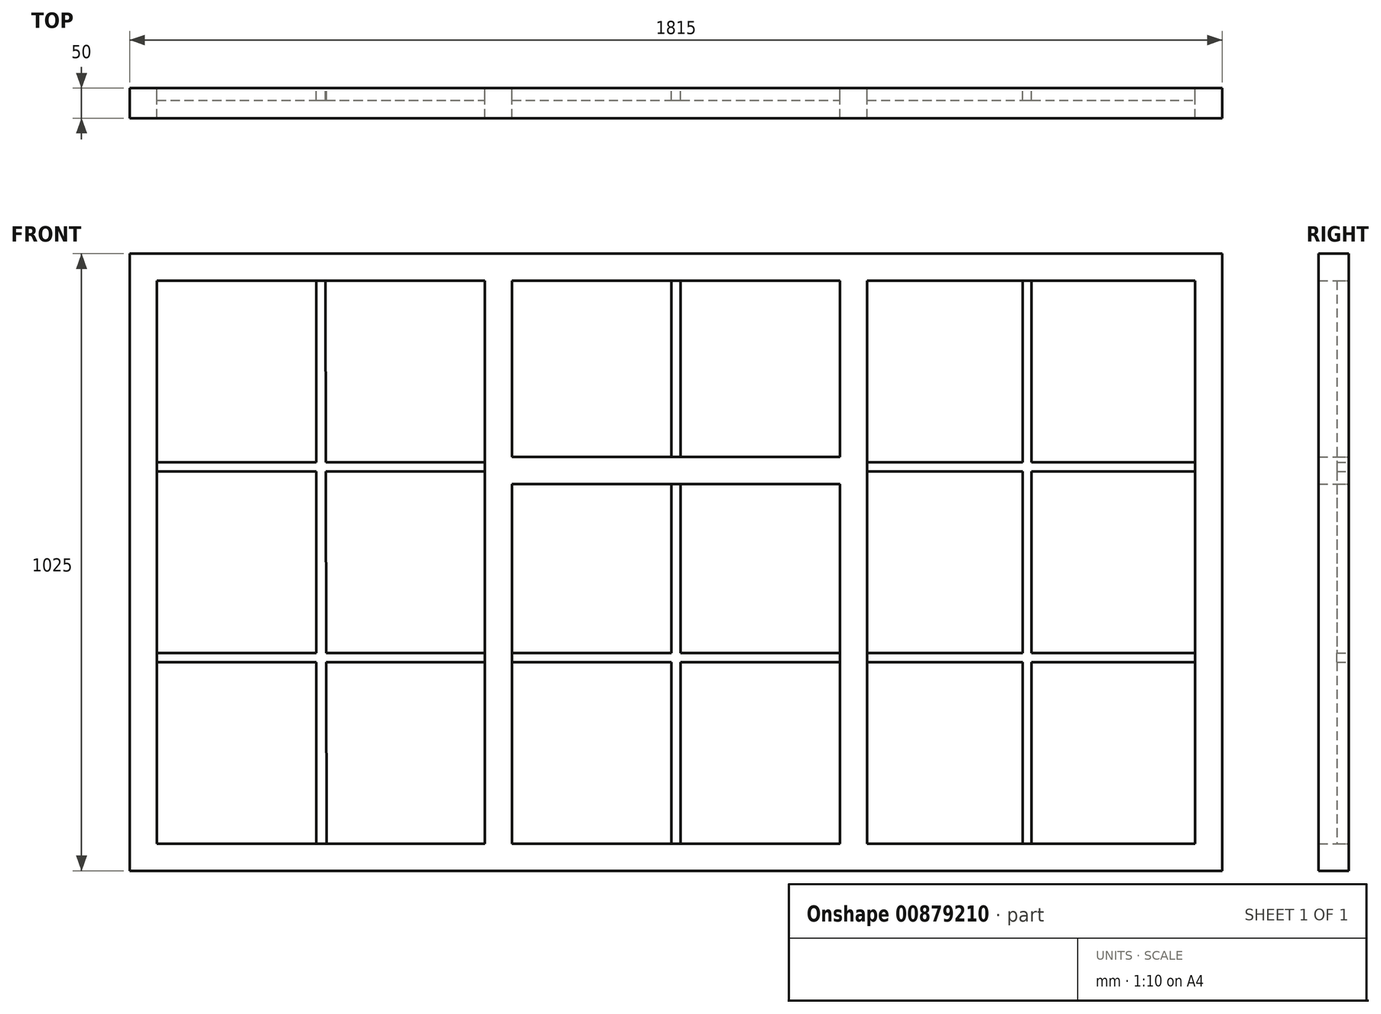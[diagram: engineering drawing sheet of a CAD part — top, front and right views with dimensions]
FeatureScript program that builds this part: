
annotation { "Feature Type Name" : "Feature", "Feature Type Description" : "" }
export const myFeature = defineFeature(function(context is Context, id is Id, definition is map)
    precondition{}
    {
        {
            var Q0;
            Q0=qCreatedBy(makeId("Front.planeOp"),FACE);
            var sketch = newSketch(context, id + "F0", { "sketchPlane" : qUnion([Q0])});
            skLineSegment(sketch, "E0.bottom", {"start": v(0, 0) * mm, "end": v(1815, 0) * mm});
            skLineSegment(sketch, "E0.top", {"start": v(0, 1025) * mm, "end": v(1815, 1025) * mm});
            skLineSegment(sketch, "E0.left", {"start": v(0, 0) * mm, "end": v(0, 1025) * mm});
            skLineSegment(sketch, "E0.right", {"start": v(1815, 0) * mm, "end": v(1815, 1025) * mm});
            skLineSegment(sketch, "E1.bottom", {"start": v(45, 980) * mm, "end": v(590, 980) * mm});
            skLineSegment(sketch, "E1.top", {"start": v(45, 45) * mm, "end": v(590, 45) * mm});
            skLineSegment(sketch, "E1.left", {"start": v(45, 980) * mm, "end": v(45, 45) * mm});
            skLineSegment(sketch, "E1.right", {"start": v(590, 980) * mm, "end": v(590, 45) * mm});
            skLineSegment(sketch, "E2.bottom", {"start": v(635, 980) * mm, "end": v(1180, 980) * mm});
            skLineSegment(sketch, "E2.top", {"start": v(635, 687.5) * mm, "end": v(1180, 687.5) * mm});
            skLineSegment(sketch, "E2.left", {"start": v(635, 980) * mm, "end": v(635, 687.5) * mm});
            skLineSegment(sketch, "E2.right", {"start": v(1180, 980) * mm, "end": v(1180, 687.5) * mm});
            skLineSegment(sketch, "E3.bottom", {"start": v(635, 642.5) * mm, "end": v(1180, 642.5) * mm});
            skLineSegment(sketch, "E3.top", {"start": v(635, 45) * mm, "end": v(1180, 45) * mm});
            skLineSegment(sketch, "E3.left", {"start": v(635, 642.5) * mm, "end": v(635, 45) * mm});
            skLineSegment(sketch, "E3.right", {"start": v(1180, 642.5) * mm, "end": v(1180, 45) * mm});
            skLineSegment(sketch, "E4.bottom", {"start": v(1225, 980) * mm, "end": v(1770, 980) * mm});
            skLineSegment(sketch, "E4.top", {"start": v(1225, 45) * mm, "end": v(1770, 45) * mm});
            skLineSegment(sketch, "E4.left", {"start": v(1225, 980) * mm, "end": v(1225, 45) * mm});
            skLineSegment(sketch, "E4.right", {"start": v(1770, 980) * mm, "end": v(1770, 45) * mm});
            skSolve(sketch);
        }
        {
            var Q0;
            Q0=qSketchRegion(id+"F0",true);
            extrude(context, id + "F1", {"entities" : qUnion([Q0]), "depth" : 50 * mm, "offsetDistance" : 25 * mm});
        }
        {
            var Q0;
            Q0=qCreatedBy(makeId("Front.planeOp"),FACE);
            var sketch = newSketch(context, id + "F2", { "sketchPlane" : qUnion([Q0])});
            skLineSegment(sketch, "E5.bottom", {"start": v(310, 980) * mm, "end": v(325, 980) * mm});
            skLineSegment(sketch, "E5.top", {"start": v(310, 45) * mm, "end": v(327.01, 45) * mm});
            skLineSegment(sketch, "E6.bottom", {"start": v(45, 678.33) * mm, "end": v(310, 678.33) * mm});
            skLineSegment(sketch, "E6.top", {"start": v(45, 663.33) * mm, "end": v(310, 663.33) * mm});
            skLineSegment(sketch, "E6.left", {"start": v(45, 678.33) * mm, "end": v(45, 663.33) * mm});
            skLineSegment(sketch, "E6.right", {"start": v(590, 678.33) * mm, "end": v(590, 663.33) * mm});
            skLineSegment(sketch, "E7.bottom", {"start": v(45, 361.67) * mm, "end": v(310, 361.67) * mm});
            skLineSegment(sketch, "E7.top", {"start": v(45, 346.67) * mm, "end": v(310, 346.67) * mm});
            skLineSegment(sketch, "E7.left", {"start": v(45, 361.67) * mm, "end": v(45, 346.67) * mm});
            skLineSegment(sketch, "E7.right", {"start": v(590, 361.67) * mm, "end": v(590, 346.67) * mm});
            skLineSegment(sketch, "E8.trimOffspring", {"start": v(325, 980) * mm, "end": v(325.65, 678.33) * mm});
            skLineSegment(sketch, "E9.trimOffspring", {"start": v(310, 980) * mm, "end": v(310, 678.33) * mm});
            skLineSegment(sketch, "E10.trimOffspring", {"start": v(325.65, 678.33) * mm, "end": v(590, 678.33) * mm});
            skLineSegment(sketch, "E11.trimOffspring", {"start": v(310, 663.33) * mm, "end": v(310, 361.67) * mm});
            skLineSegment(sketch, "E12.trimOffspring", {"start": v(325.68, 663.33) * mm, "end": v(590, 663.33) * mm});
            skLineSegment(sketch, "E13.trimOffspring", {"start": v(325.68, 663.33) * mm, "end": v(326.33, 361.67) * mm});
            skLineSegment(sketch, "E14.trimOffspring", {"start": v(326.33, 361.67) * mm, "end": v(590, 361.67) * mm});
            skLineSegment(sketch, "E15.trimOffspring", {"start": v(310, 346.67) * mm, "end": v(310, 45) * mm});
            skLineSegment(sketch, "E16.trimOffspring", {"start": v(326.36, 346.67) * mm, "end": v(590, 346.67) * mm});
            skLineSegment(sketch, "E17.trimOffspring", {"start": v(326.36, 346.67) * mm, "end": v(327.01, 45) * mm});
            skLineSegment(sketch, "E18.bottom", {"start": v(1483.1, 980) * mm, "end": v(1498.1, 980) * mm});
            skLineSegment(sketch, "E18.top", {"start": v(1483.1, 45) * mm, "end": v(1498.1, 45) * mm});
            skLineSegment(sketch, "E18.left", {"start": v(1483.1, 980) * mm, "end": v(1483.1, 678.33) * mm});
            skLineSegment(sketch, "E18.right", {"start": v(1498.1, 980) * mm, "end": v(1498.1, 678.33) * mm});
            skLineSegment(sketch, "E19.bottom", {"start": v(1225, 678.33) * mm, "end": v(1483.1, 678.33) * mm});
            skLineSegment(sketch, "E19.top", {"start": v(1225, 663.33) * mm, "end": v(1483.1, 663.33) * mm});
            skLineSegment(sketch, "E19.left", {"start": v(1225, 678.33) * mm, "end": v(1225, 663.33) * mm});
            skLineSegment(sketch, "E19.right", {"start": v(1770, 678.33) * mm, "end": v(1770, 663.33) * mm});
            skLineSegment(sketch, "E20.bottom", {"start": v(1225, 346.67) * mm, "end": v(1483.1, 346.67) * mm});
            skLineSegment(sketch, "E20.top", {"start": v(1225, 361.67) * mm, "end": v(1483.1, 361.67) * mm});
            skLineSegment(sketch, "E20.left", {"start": v(1225, 346.67) * mm, "end": v(1225, 361.67) * mm});
            skLineSegment(sketch, "E20.right", {"start": v(1770, 346.67) * mm, "end": v(1770, 361.67) * mm});
            skLineSegment(sketch, "E21.trimOffspring", {"start": v(1483.1, 663.33) * mm, "end": v(1483.1, 361.67) * mm});
            skLineSegment(sketch, "E22.trimOffspring", {"start": v(1498.1, 678.33) * mm, "end": v(1770, 678.33) * mm});
            skLineSegment(sketch, "E23.trimOffspring", {"start": v(1498.1, 663.33) * mm, "end": v(1498.1, 361.67) * mm});
            skLineSegment(sketch, "E24.trimOffspring", {"start": v(1498.1, 663.33) * mm, "end": v(1770, 663.33) * mm});
            skLineSegment(sketch, "E25.trimOffspring", {"start": v(1498.1, 361.67) * mm, "end": v(1770, 361.67) * mm});
            skLineSegment(sketch, "E26.trimOffspring", {"start": v(1483.1, 346.67) * mm, "end": v(1483.1, 45) * mm});
            skLineSegment(sketch, "E27.trimOffspring", {"start": v(1498.1, 346.67) * mm, "end": v(1770, 346.67) * mm});
            skLineSegment(sketch, "E28.trimOffspring", {"start": v(1498.1, 346.67) * mm, "end": v(1498.1, 45) * mm});
            skLineSegment(sketch, "E29.bottom", {"start": v(900, 980) * mm, "end": v(915, 980) * mm});
            skLineSegment(sketch, "E29.top", {"start": v(900, 687.5) * mm, "end": v(915, 687.5) * mm});
            skLineSegment(sketch, "E29.left", {"start": v(900, 980) * mm, "end": v(900, 687.5) * mm});
            skLineSegment(sketch, "E29.right", {"start": v(915, 980) * mm, "end": v(915, 687.5) * mm});
            skLineSegment(sketch, "E30.bottom", {"start": v(900, 642.5) * mm, "end": v(915, 642.5) * mm});
            skLineSegment(sketch, "E30.top", {"start": v(900, 45) * mm, "end": v(915, 45) * mm});
            skLineSegment(sketch, "E30.left", {"start": v(900, 642.5) * mm, "end": v(900, 361.67) * mm});
            skLineSegment(sketch, "E30.right", {"start": v(915, 642.5) * mm, "end": v(915, 361.67) * mm});
            skLineSegment(sketch, "E31.bottom", {"start": v(635, 361.67) * mm, "end": v(900, 361.67) * mm});
            skLineSegment(sketch, "E31.top", {"start": v(635, 346.67) * mm, "end": v(900, 346.67) * mm});
            skLineSegment(sketch, "E31.left", {"start": v(635, 361.67) * mm, "end": v(635, 346.67) * mm});
            skLineSegment(sketch, "E31.right", {"start": v(1180, 361.67) * mm, "end": v(1180, 346.67) * mm});
            skLineSegment(sketch, "E32.trimOffspring", {"start": v(915, 361.67) * mm, "end": v(1180, 361.67) * mm});
            skLineSegment(sketch, "E33.trimOffspring", {"start": v(900, 346.67) * mm, "end": v(900, 45) * mm});
            skLineSegment(sketch, "E34.trimOffspring", {"start": v(915, 346.67) * mm, "end": v(1180, 346.67) * mm});
            skLineSegment(sketch, "E35.trimOffspring", {"start": v(915, 346.67) * mm, "end": v(915, 45) * mm});
            skSolve(sketch);
        }
        {
            var Q0;
            Q0=qSketchRegion(id+"F2",true);
            extrude(context, id + "F3", {"entities" : qUnion([Q0]), "operationType" : NewBodyOperationType.ADD, "depth" : 20 * mm, "offsetDistance" : 25 * mm});
        }
    });
